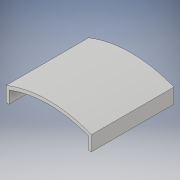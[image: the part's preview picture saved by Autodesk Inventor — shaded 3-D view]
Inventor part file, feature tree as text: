
AUTODESK INVENTOR PART (.ipt)
format: ipt  version: 2019 (Build 230136000, 136)  size: 104,960 bytes
history: native  units: in
note: dims shown in document units (in); Inventor stores cm internally (conversion verified against a paired STEP export)
features: extrude x1, sketch x1
ambient origin geometry x8: Origin, YZ Plane, XZ Plane, XY Plane, X Axis, Y Axis, Z Axis, Center Point
bodies: Solid1 (feature_tree)
feature tree (2):
  extrude  "Extrusion1"  Depth=0.5in
  sketch  "Sketch1"  dims[d0=0.125in d1=0.5in d2=3.22in d3=0.125in d4=0.5in d5=0.0997in d6=0.0997in d7=3.35in d8=0.0in]
